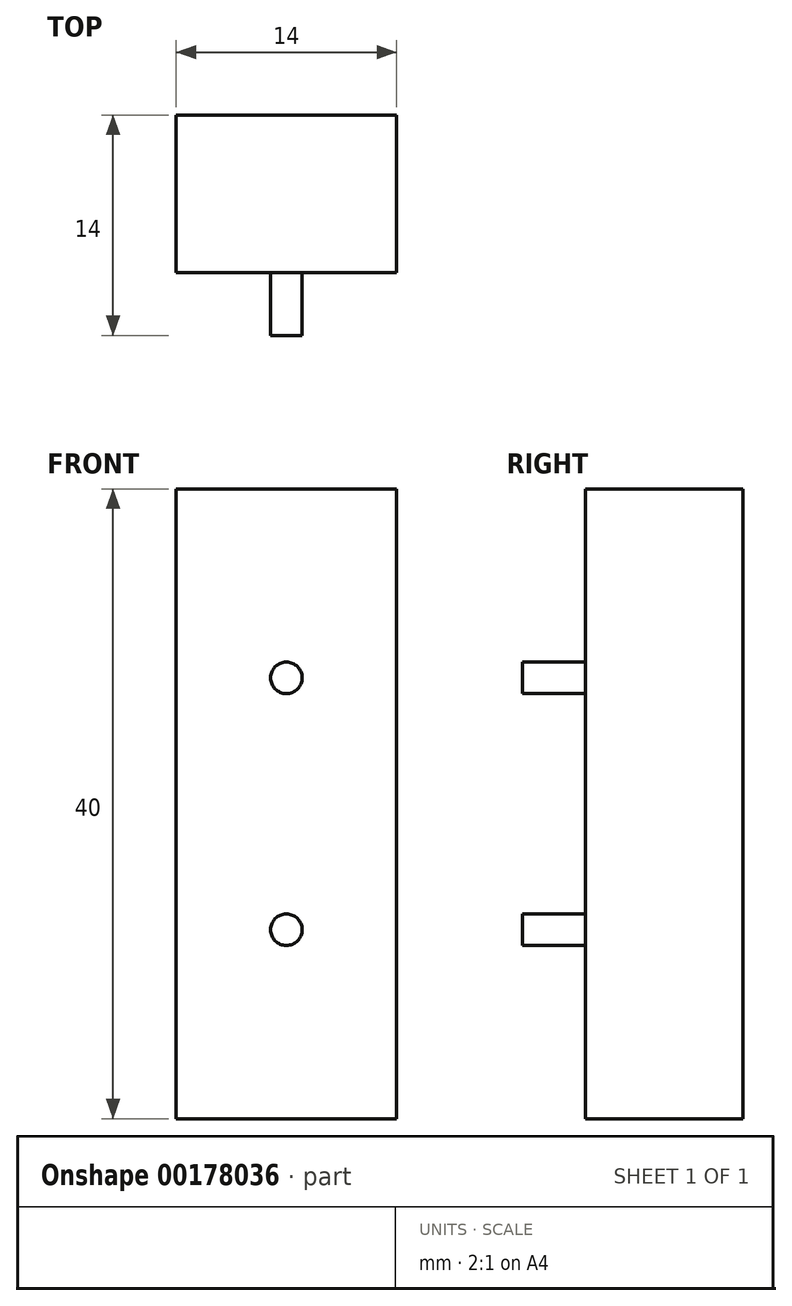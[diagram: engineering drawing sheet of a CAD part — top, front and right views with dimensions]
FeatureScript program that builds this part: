
annotation { "Feature Type Name" : "Feature", "Feature Type Description" : "" }
export const myFeature = defineFeature(function(context is Context, id is Id, definition is map)
    precondition{}
    {
        {
            var Q0;
            Q0=qCreatedBy(makeId("Right.planeOp"),FACE);
            var sketch = newSketch(context, id + "F0", { "sketchPlane" : qUnion([Q0])});
            skLineSegment(sketch, "E0.bottom", {"start": v(5, -20) * mm, "end": v(-5, -20) * mm});
            skLineSegment(sketch, "E0.top", {"start": v(5, 20) * mm, "end": v(-5, 20) * mm});
            skLineSegment(sketch, "E0.left", {"start": v(5, -20) * mm, "end": v(5, 20) * mm});
            skLineSegment(sketch, "E0.right", {"start": v(-5, -20) * mm, "end": v(-5, 20) * mm});
            skPoint(sketch, "E0.middle", {"position": v(0, 0) * mm});
            skSolve(sketch);
        }
        {
            var Q0;
            Q0=makeQuery(id+"F0.imprint","IMPRINT",FACE,{"disambiguationData":[TD([[makeQuery(id+"F0.imprint","IMPRINT",EDGE,{"derivedFrom":sQuery(id+"F0.wireOp",EDGE,"E0.bottom")}),-1.0]])]});
            extrude(context, id + "F1", {"entities" : qUnion([Q0]), "depth" : 7 * mm, "hasSecondDirection" : true, "secondDirectionOppositeDirection" : true, "secondDirectionDepth" : 7 * mm});
        }
        {
            var Q0;
            Q0=makeQuery(id+"F1.opExtrude","SWEPT_FACE",FACE,{"disambiguationData":[OSD([sQuery(id+"F0.wireOp",EDGE,"E0.right")])]});
            var sketch = newSketch(context, id + "F2", { "sketchPlane" : qUnion([Q0])});
            skCircle(sketch, "E1", {"center": v(0, 8) * mm, "radius": 1 * mm});
            skCircle(sketch, "E2", {"center": v(0, -8) * mm, "radius": 1 * mm});
            skSolve(sketch);
        }
        {
            var Q0;
            Q0 = qSketchRegion(id + "F2", true);
            extrude(context, id + "F3", {"entities" : qUnion([Q0]), "operationType" : NewBodyOperationType.ADD, "depth" : 4 * mm});
        }
    });
